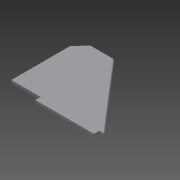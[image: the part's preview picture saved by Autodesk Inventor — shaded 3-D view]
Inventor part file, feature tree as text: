
AUTODESK INVENTOR PART (.ipt)
format: ipt  version: 2014 SP1 (Build 180222100, 222)  size: 81,920 bytes
history: native  units: mm
features: extrude x1, fillet x1, sketch x1
ambient origin geometry x8: Origin, YZ Plane, XZ Plane, XY Plane, X Axis, Y Axis, Z Axis, Center Point
bodies: Solid1 (feature_tree)
feature tree (3):
  extrude  "Extrusion1"  Depth=2.5mm
  fillet  "Fillet1"  Radius=175.0mm
  sketch  "Sketch1"  dims[d1=110.0mm d5=45.0mm d6=175.0mm d7=10.0mm d8=10.0mm d9=110.0mm d10=5.0mm d11=0.0mm d12=2.5mm]
